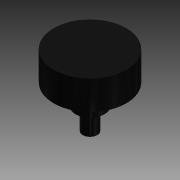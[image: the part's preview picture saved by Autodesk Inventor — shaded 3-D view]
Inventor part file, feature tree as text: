
AUTODESK INVENTOR PART (.ipt)
format: ipt  version: 2013 (Build 170138000, 138)  size: 85,504 bytes
history: native  units: in
note: dims shown in document units (in); Inventor stores cm internally (conversion verified against a paired STEP export)
features: revolve x1, other x1, imported_body x1
ambient origin geometry x8: Origin, YZ Plane, XZ Plane, XY Plane, X Axis, Y Axis, Z Axis, Center Point
feature tree (3):
  revolve  "Revolve1"  [1 undecoded]
  other  "Grahill Encoder1"
  imported_body  "Base1"
note: 1 required parameter value undecoded (feature->parameter linkage not recoverable at this tier; creation-order binding heuristic only, values carry confidence <= 0.55)
